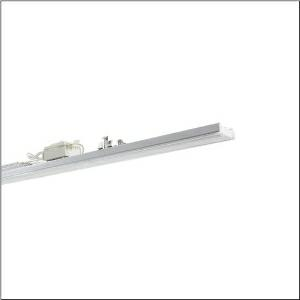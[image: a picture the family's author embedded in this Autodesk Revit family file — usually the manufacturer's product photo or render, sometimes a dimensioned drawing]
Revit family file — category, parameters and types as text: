
# Revit family: licross_11_recessed_ho_51tl12dn4exm3s4
name_source: partatom
category: Lighting Fixtures
units: mm (PartAtom-declared; Revit-internal decimal feet)

## family parameters
Cut with Voids When Loaded = No
Host = Face
Light Source = No
Part Type = Normal
Room Calculation Point = No
Round Connector Dimension = Use Diameter
Shared = No

## types (1)
- --- (1 x LED, 1000 lm, 7.2 W, 4000K)
    Apparent Load = 7 VA
    CIE Flux Codes = 66 91 98 100 100
    Color Rendering = 80
    Color Temperature = 4000K
    Default Elevation = 1800 mm
    Description = Licross 11 Recessed HO, luminaire insert, of sheet steel, coil coated, white, length: 1.500mm, width: 66mm, height: 67mm, LED rated luminous flux: 14.030lm, light colour: 840, SDCM (Standard Deviation of Colour Matching)MacAdam ≤ 2 SDCM (initial), control gear: DALI 2, with plug, 6-pole, with phase selection, for trunking rail, 9 or 11-core, mains connection: 220..240V, AC, 50/60Hz, rated input power: 81W, for trunking rail, 9-/11-core, internal wiring halogen-free, for emergency light function, converter,control gear: single battery element, battery: LiFePO4, 9Ah, primary optical cover: cover, of PMMA, light emission: direct distribution, primary light characteristic: symmetric, protection rating (complete): IP40, insulation class (complete): insulation class I (protective earthing), certification: CE, UKCA, protection symbol: D if used in an environment without relevant dust loads with corresponding accessories, impact resistance: IK06, permissible ambient temperature for indoor applications: +5..+30°C, standard: EN 60598-2-22, LABS conformity tested according to VDMA 24364:2018-05, reducing of maximum allowable ambient temperature of 5°C with ceiling mounting, corresponds to IFS (International Featured Standards) requirements for safety and quality in the food industry, The light source and the operating device comply with the requirements of the Ecodesign Regulation (EU) 2019/2020 and are replaceable in accordance with this regulation, packaging unit: 1 piece
    Height = 58 mm
    Lamp = 1 x LED
    Lamp Light Flux = 1000 lm
    Lamp Power = 7.2 W
    Lamp count = 1
    Length = 1500 mm
    Luminous efficacy = 139 lm/W
    Manufacturer = Siteco
    ModVariant = No
    Model = 51TL12DN4EXM3S4
    Mounting Place = Ceiling
    Mounting Type = Pendant
    Number of Poles = 1
    OnlyDefault = Yes
    Power Factor = 1
    Product Name = Licross 11 Recessed HO
    Product group = luminaire insert | ceiling pendant
    ProductGroupID = 901
    Protection Class = Protection class I
    Protection Degree = IP 40
    RLX_Detail_Level = 1
    RLX_Emergency_Light_Flux = 0 lm
    RLX_Emergency_Type = 0
    RLX_Emergency_Type_DB = No
    RlxData = <blob elided: 25237 chars, md5=57da5903>
    Socket = socket
    Standby Power = 0 W
    System Light Flux = 1000 lm
    System Power = 7 W
    Type Comments = : emergency light operation: 3 h
    Type Image = l_1296930.jpg
    URL = http://relux.com
    VarID = @adj_093753
    Voltage = 0 V
    Weight = 0.00 kg
    Width = 66 mm

## geometry (parser evidence)
native form markers: Blend x4, Sweep x11
no freeform markers — native parametric forms only
